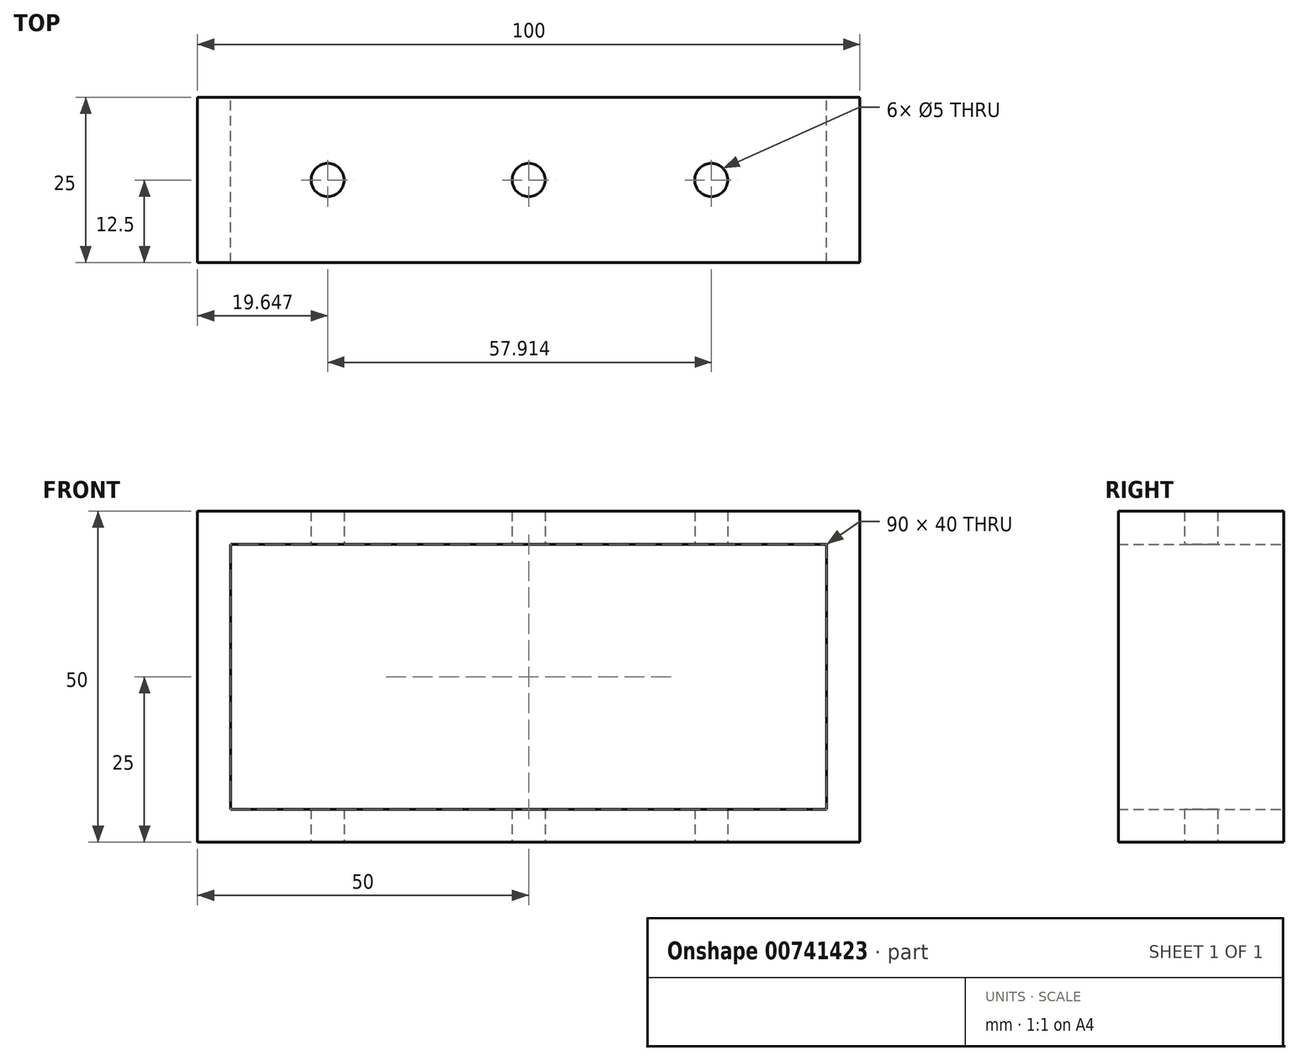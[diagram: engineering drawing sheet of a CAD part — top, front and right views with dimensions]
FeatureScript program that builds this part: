
annotation { "Feature Type Name" : "Feature", "Feature Type Description" : "" }
export const myFeature = defineFeature(function(context is Context, id is Id, definition is map)
    precondition{}
    {
        {
            var Q0;
            Q0=qCreatedBy(makeId("Front.planeOp"),FACE);
            var sketch = newSketch(context, id + "F0", { "sketchPlane" : qUnion([Q0])});
            skLineSegment(sketch, "E0.bottom", {"start": v(50, 25) * mm, "end": v(-50, 25) * mm});
            skLineSegment(sketch, "E0.top", {"start": v(50, -25) * mm, "end": v(-50, -25) * mm});
            skLineSegment(sketch, "E0.left", {"start": v(50, 25) * mm, "end": v(50, -25) * mm});
            skLineSegment(sketch, "E0.right", {"start": v(-50, 25) * mm, "end": v(-50, -25) * mm});
            skPoint(sketch, "E0.middle", {"position": v(0, 0) * mm});
            skLineSegment(sketch, "E1.bottom", {"start": v(45, 20) * mm, "end": v(-45, 20) * mm});
            skLineSegment(sketch, "E1.top", {"start": v(45, -20) * mm, "end": v(-45, -20) * mm});
            skLineSegment(sketch, "E1.left", {"start": v(45, 20) * mm, "end": v(45, -20) * mm});
            skLineSegment(sketch, "E1.right", {"start": v(-45, 20) * mm, "end": v(-45, -20) * mm});
            skSolve(sketch);
        }
        {
            var Q0;
            Q0=makeQuery(id+"F0.imprint","IMPRINT",FACE,{"disambiguationData":[TD([[makeQuery(id+"F0.imprint","IMPRINT",EDGE,{"derivedFrom":sQuery(id+"F0.wireOp",EDGE,"E0.bottom")}),1.0]])]});
            extrude(context, id + "F1", {"entities" : qUnion([Q0]), "depth" : 25 * mm, "offsetDistance" : 25.4 * mm});
        }
        {
            var Q0;
            Q0=makeQuery(id+"F1.opExtrude","SWEPT_FACE",FACE,{"disambiguationData":[OSD([sQuery(id+"F0.wireOp",EDGE,"E0.top")])]});
            var sketch = newSketch(context, id + "F2", { "sketchPlane" : qUnion([Q0])});
            skCircle(sketch, "E2", {"center": v(0, 12.5) * mm, "radius": 2.5 * mm});
            skPoint(sketch, "E2.centerSnap0", {"position": v(-50, 12.5) * mm});
            skCircle(sketch, "E3", {"center": v(-30.35, 12.5) * mm, "radius": 2.5 * mm});
            skCircle(sketch, "E4", {"center": v(27.56, 12.5) * mm, "radius": 2.5 * mm});
            skSolve(sketch);
        }
        {
            var Q0;
            Q0 = qSketchRegion(id + "F2", true);
            extrude(context, id + "F3", {"entities" : qUnion([Q0]), "operationType" : NewBodyOperationType.REMOVE, "endBound" : BoundingType.THROUGH_ALL, "oppositeDirection" : true, "depth" : 25.4 * mm, "offsetDistance" : 25.4 * mm});
        }
    });
